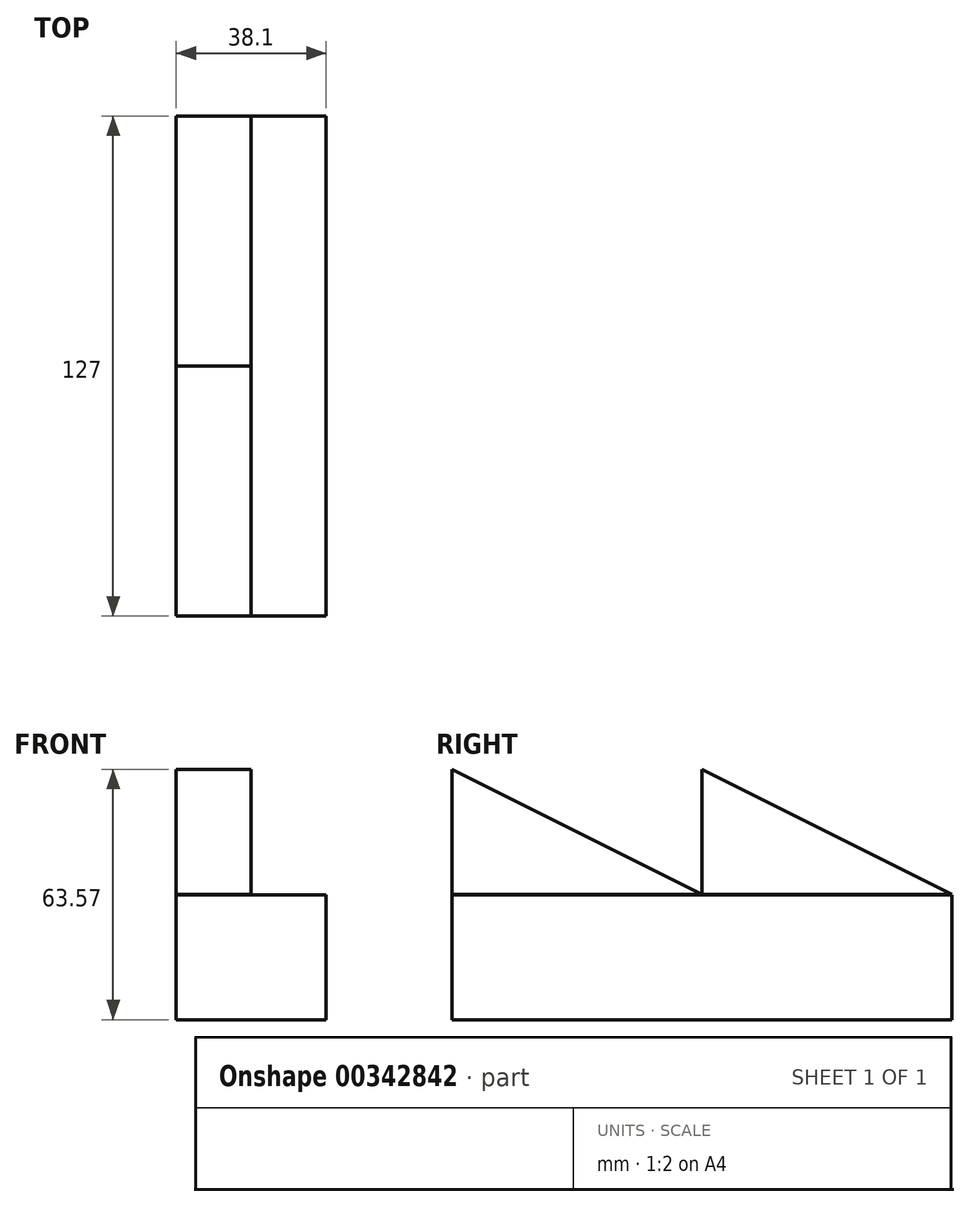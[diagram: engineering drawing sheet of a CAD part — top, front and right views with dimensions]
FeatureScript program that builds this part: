
annotation { "Feature Type Name" : "Feature", "Feature Type Description" : "" }
export const myFeature = defineFeature(function(context is Context, id is Id, definition is map)
    precondition{}
    {
        {
            var Q0;
            Q0=qCreatedBy(makeId("Front.planeOp"),FACE);
            var sketch = newSketch(context, id + "F0", { "sketchPlane" : qUnion([Q0])});
            skLineSegment(sketch, "E0.bottom", {"start": v(-19.05, -15.87) * mm, "end": v(19.05, -15.87) * mm});
            skLineSegment(sketch, "E0.top", {"start": v(-19.05, 15.88) * mm, "end": v(19.05, 15.88) * mm});
            skLineSegment(sketch, "E0.left", {"start": v(-19.05, -15.87) * mm, "end": v(-19.05, 15.88) * mm});
            skLineSegment(sketch, "E0.right", {"start": v(19.05, -15.87) * mm, "end": v(19.05, 15.88) * mm});
            skPoint(sketch, "E0.middle", {"position": v(0, 0) * mm});
            skSolve(sketch);
        }
        {
            var Q0;
            Q0=makeQuery(id+"F0.imprint","IMPRINT",FACE,{"disambiguationData":[TD([[makeQuery(id+"F0.imprint","IMPRINT",EDGE,{"derivedFrom":sQuery(id+"F0.wireOp",EDGE,"E0.bottom")}),1.0]])]});
            extrude(context, id + "F1", {"entities" : qUnion([Q0]), "depth" : 127 * mm});
        }
        {
            var Q0;
            Q0=qCreatedBy(makeId("Right.planeOp"),FACE);
            var sketch = newSketch(context, id + "F2", { "sketchPlane" : qUnion([Q0])});
            skLineSegment(sketch, "E1", {"start": v(0, 15.94) * mm, "end": v(-63.5, 15.94) * mm});
            skLineSegment(sketch, "E2", {"start": v(-63.5, 15.94) * mm, "end": v(-63.5, 47.69) * mm});
            skLineSegment(sketch, "E3", {"start": v(-63.5, 47.69) * mm, "end": v(0, 15.94) * mm});
            skLineSegment(sketch, "E4", {"start": v(-63.5, 15.94) * mm, "end": v(-127, 15.94) * mm});
            skLineSegment(sketch, "E5", {"start": v(-127, 15.94) * mm, "end": v(-127, 47.69) * mm});
            skLineSegment(sketch, "E6", {"start": v(-127, 47.69) * mm, "end": v(-63.5, 15.94) * mm});
            skSolve(sketch);
        }
        {
            var Q0;
            Q0=makeQuery(id+"F2.imprint","IMPRINT",FACE,{"disambiguationData":[TD([[makeQuery(id+"F2.imprint","IMPRINT",EDGE,{"derivedFrom":sQuery(id+"F2.wireOp",EDGE,"E1")}),-1.0]])]});
            var Q1;
            Q1=makeQuery(id+"F2.imprint","IMPRINT",FACE,{"disambiguationData":[TD([[makeQuery(id+"F2.imprint","IMPRINT",EDGE,{"derivedFrom":sQuery(id+"F2.wireOp",EDGE,"E4")}),-1.0]])]});
            extrude(context, id + "F3", {"entities" : qUnion([Q0, Q1]), "oppositeDirection" : true, "depth" : 19.05 * mm});
        }
    });
